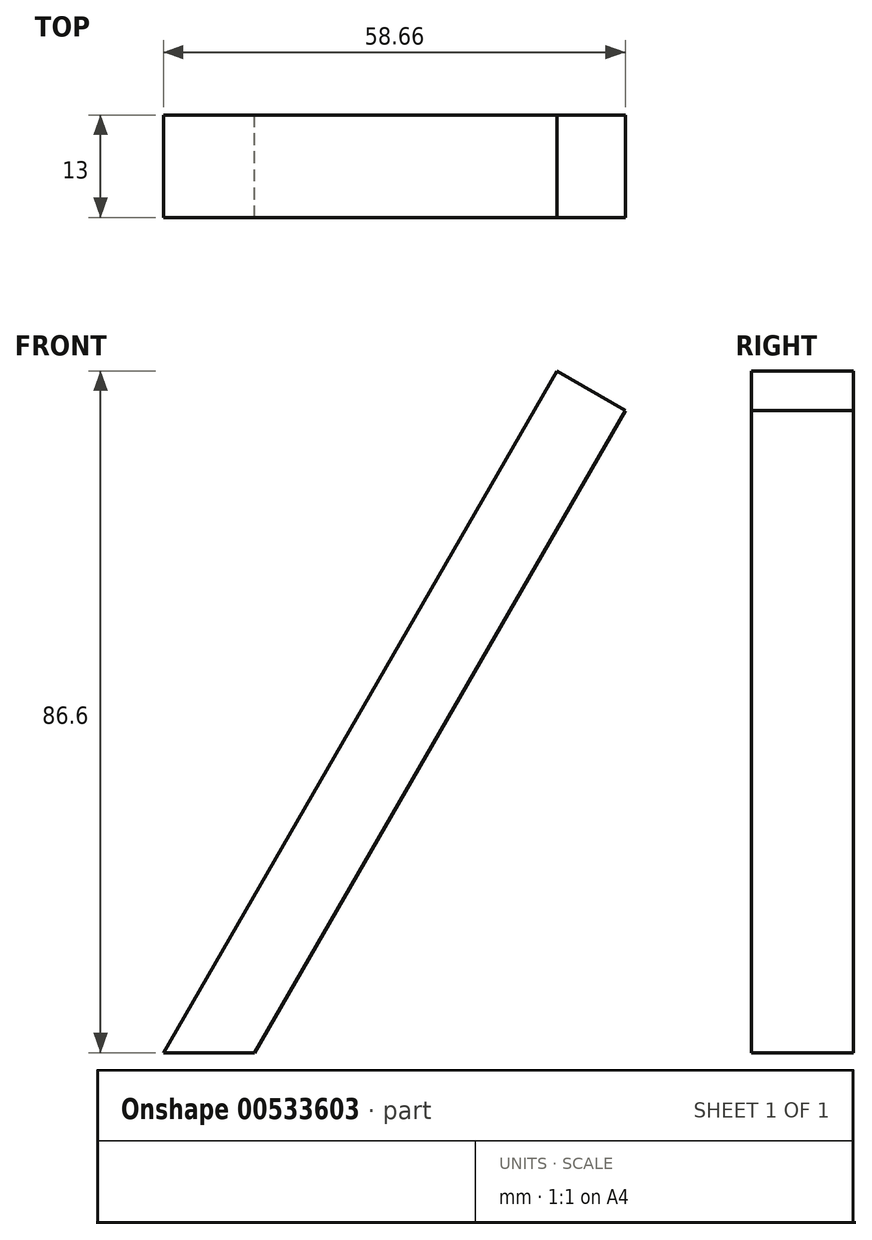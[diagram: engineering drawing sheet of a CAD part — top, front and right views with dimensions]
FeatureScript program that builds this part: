
annotation { "Feature Type Name" : "Feature", "Feature Type Description" : "" }
export const myFeature = defineFeature(function(context is Context, id is Id, definition is map)
    precondition{}
    {
        {
            var Q0;
            Q0=qCreatedBy(makeId("Front.planeOp"),FACE);
            var sketch = newSketch(context, id + "F0", { "sketchPlane" : qUnion([Q0])});
            skLineSegment(sketch, "E0", {"start": v(3, 0) * mm, "end": v(53, 86.6) * mm});
            skLineSegment(sketch, "E1", {"start": v(53, 86.6) * mm, "end": v(61.66, 81.6) * mm});
            skLineSegment(sketch, "E2", {"start": v(61.66, 81.6) * mm, "end": v(14.54, 0) * mm});
            skLineSegment(sketch, "E3", {"start": v(14.54, 0) * mm, "end": v(3, 0) * mm});
            skSolve(sketch);
        }
        {
            var Q0;
            Q0=makeQuery(id+"F0.imprint","IMPRINT",FACE,{"disambiguationData":[TD([[makeQuery(id+"F0.imprint","IMPRINT",EDGE,{"derivedFrom":sQuery(id+"F0.wireOp",EDGE,"E0")}),-1.0]])]});
            extrude(context, id + "F1", {"entities" : qUnion([Q0]), "depth" : 13 * mm});
        }
    });
